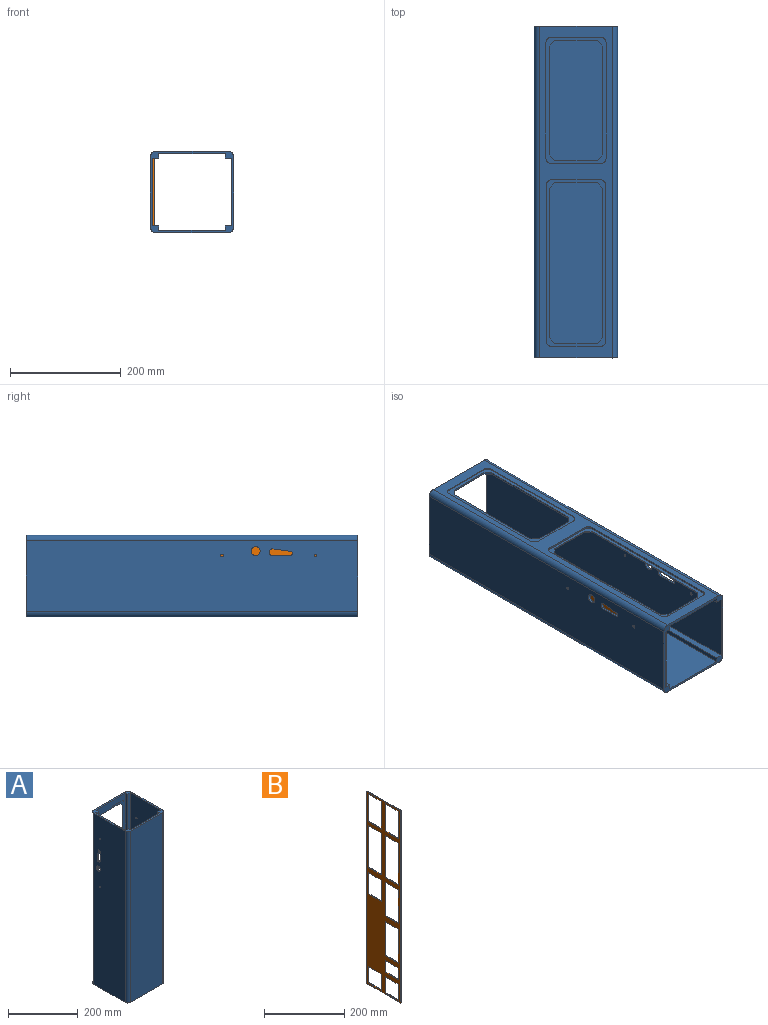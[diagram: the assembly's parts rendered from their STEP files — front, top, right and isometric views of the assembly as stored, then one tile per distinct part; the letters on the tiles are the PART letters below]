
ASSEMBLY  parts=2 mates=1
PART A: 70 faces, bbox 150.5x147.9x600 mm
  f0: plane 600x130.47mm, normal (0,1,0), area 21053.1mm2, adj f1,f19,f20,f21,f22,f23,f24,f25
  f1: cylinder r=10mm len=600mm, axis (0,0,-1), area 9424.8mm2, adj f0,f2,f20,f21
  f2: plane 600x127.9mm, normal (-1,0,0), area 76086.2mm2, adj f1,f3,f20,f21,f56,f57,f58,f59
  f3: cylinder r=10mm len=600mm, axis (0,0,-1), area 9424.8mm2, adj f2,f4,f20,f21
  f4: plane 600x130.47mm, normal (0,-1,0), area 78281.8mm2, adj f3,f5,f20,f21
  f5: cylinder r=10mm len=600mm, axis (0,0,-1), area 9424.8mm2, adj f4,f6,f20,f21
  f6: plane 600x127.9mm, normal (1,0,0), area 76086.2mm2, adj f5,f19,f20,f21,f63,f64,f65,f66
  f7: plane 600x8.22mm, normal (1,0,0), area 4932mm2, adj f8,f18,f20,f21
  f8: plane 600x119.67mm, normal (0,-1,0), area 23393.6mm2, adj f7,f9,f20,f21,f31,f32,f33,f34
  f9: plane 600x8.22mm, normal (-1,0,0), area 4932mm2, adj f8,f10,f20,f21
  f10: plane 600x11.05mm, normal (0,-1,0), area 6630mm2, adj f9,f11,f20,f21
  f11: plane 600x122.76mm, normal (-1,0,0), area 73002.2mm2, adj f10,f12,f20,f21,f63,f64,f65,f66
  f12: plane 600x11.05mm, normal (0,1,0), area 6630mm2, adj f11,f13,f20,f21
  f13: plane 600x8.22mm, normal (-1,0,0), area 4932mm2, adj f12,f14,f20,f21
  f14: plane 600x119.67mm, normal (0,1,0), area 71801.8mm2, adj f13,f15,f20,f21
  f15: plane 600x8.22mm, normal (1,0,0), area 4932mm2, adj f14,f16,f20,f21
  f16: plane 600x11.05mm, normal (0,1,0), area 6630mm2, adj f15,f17,f20,f21
  f17: plane 600x122.76mm, normal (1,0,0), area 73002.2mm2, adj f16,f18,f20,f21,f56,f57,f58,f59
  f18: plane 600x11.05mm, normal (0,-1,0), area 6630mm2, adj f7,f17,f20,f21
  f19: cylinder r=10mm len=600mm, axis (0,0,-1), area 9424.8mm2, adj f0,f6,f20,f21
  f20: plane 150.47x147.9mm, normal (0,0,1), area 2797.6mm2, adj f0,f1,f2,f3,f4,f5,f6,f7
  f21: plane 150.47x147.9mm, normal (0,0,-1), area 2797.6mm2, adj f0,f1,f2,f3,f4,f5,f6,f7
  f22: plane 208.6x1.35mm, normal (1,0,0), area 281.6mm2, adj f0,f23,f29,f30
  f23: cylinder r=10mm len=10mm, axis (0,1,0), area 21.2mm2, adj f0,f22,f24,f30
  f24: plane 88.66x1.35mm, normal (0,0,-1), area 119.7mm2, adj f0,f23,f25,f30
  f25: cylinder r=10mm len=10mm, axis (0,1,0), area 21.2mm2, adj f0,f24,f26,f30
  f26: plane 208.6x1.35mm, normal (-1,0,0), area 281.6mm2, adj f0,f25,f27,f30
  f27: cylinder r=10mm len=10mm, axis (0,1,0), area 21.2mm2, adj f0,f26,f28,f30
  f28: plane 88.66x1.35mm, normal (0,0,1), area 119.7mm2, adj f0,f27,f29,f30
  f29: cylinder r=10mm len=10mm, axis (0,1,0), area 21.2mm2, adj f0,f22,f28,f30
  f30: plane 228.6x108.66mm, normal (0,1,0), area 4041.3mm2, adj f22,f23,f24,f25,f26,f27,f28,f29
  f31: plane 76.46x3mm, normal (0,0,1), area 229.4mm2, adj f8,f30,f32,f38
  f32: plane 10x10mm, normal (-0.71,0,0.71), area 42.4mm2, adj f8,f30,f31,f33
  f33: plane 196.8x3mm, normal (-1,0,0), area 590.4mm2, adj f8,f30,f32,f34
  f34: plane 10x10mm, normal (-0.71,0,-0.71), area 42.4mm2, adj f8,f30,f33,f35
  f35: plane 76.46x3mm, normal (0,0,-1), area 229.4mm2, adj f8,f30,f34,f36
  f36: plane 10x10mm, normal (0.71,0,-0.71), area 42.4mm2, adj f8,f30,f35,f37
  f37: plane 196.8x3mm, normal (1,0,0), area 590.4mm2, adj f8,f30,f36,f38
  f38: plane 10x10mm, normal (0.71,0,0.71), area 42.4mm2, adj f8,f30,f31,f37
  f39: cylinder r=10mm len=10mm, axis (0,1,0), area 47.1mm2, adj f0,f40,f46,f47
  f40: plane 87.95x3mm, normal (0,0,1), area 263.9mm2, adj f0,f39,f41,f47
  f41: cylinder r=10mm len=10mm, axis (0,1,0), area 47.1mm2, adj f0,f40,f42,f47
  f42: plane 281.63x3mm, normal (-1,0,0), area 844.9mm2, adj f0,f41,f43,f47
  f43: cylinder r=10mm len=10mm, axis (0,1,0), area 47.1mm2, adj f0,f42,f44,f47
  f44: plane 87.95x3mm, normal (0,0,-1), area 263.9mm2, adj f0,f43,f45,f47
  f45: cylinder r=10mm len=10mm, axis (0,1,0), area 47.1mm2, adj f0,f44,f46,f47
  f46: plane 281.63x3mm, normal (1,0,0), area 844.9mm2, adj f0,f39,f45,f47
  f47: plane 301.63x107.95mm, normal (0,1,0), area 4779.2mm2, adj f39,f40,f41,f42,f43,f44,f45,f46
  f48: plane 76.08x1.35mm, normal (0,0,1), area 102.7mm2, adj f8,f47,f49,f55
  f49: plane 10x10mm, normal (-0.71,0,0.71), area 19.1mm2, adj f8,f47,f48,f50
  f50: plane 270.34x1.35mm, normal (-1,0,0), area 365mm2, adj f8,f47,f49,f51
  f51: plane 10x10mm, normal (-0.71,0,-0.71), area 19.1mm2, adj f8,f47,f50,f52
  f52: plane 76.08x1.35mm, normal (0,0,-1), area 102.7mm2, adj f8,f47,f51,f53
  f53: plane 10x10mm, normal (0.71,0,-0.71), area 19.1mm2, adj f8,f47,f52,f54
  f54: plane 270.34x1.35mm, normal (1,0,0), area 365mm2, adj f8,f47,f53,f55
  f55: plane 10x10mm, normal (0.71,0,0.71), area 19.1mm2, adj f8,f47,f48,f54
  f56: cylinder r=8.15mm len=16.3mm, axis (1,0,0), area 222.8mm2, adj f2,f17
  f57: plane 30.83x4.35mm, normal (0,1,0), area 134.1mm2, adj f2,f17,f58,f60
  f58: cylinder r=6.17mm len=12.34mm, axis (1,0,0), area 93.5mm2, adj f2,f17,f57,f59
  f59: plane 30.55x4.35mm, normal (0,-0.99,-0.13), area 134.1mm2, adj f2,f17,f58,f60
  f60: cylinder r=4.05mm len=8.1mm, axis (1,0,0), area 58.5mm2, adj f2,f17,f57,f59
  f61: cylinder r=2.45mm len=4.9mm, axis (1,0,0), area 67mm2, adj f2,f17
  f62: cylinder r=2.45mm len=4.9mm, axis (1,0,0), area 67mm2, adj f2,f17
  f63: cylinder r=8.15mm len=16.3mm, axis (1,0,0), area 222.8mm2, adj f6,f11
  f64: cylinder r=4.05mm len=8.1mm, axis (1,0,0), area 58.5mm2, adj f6,f11,f65,f67
  f65: plane 30.55x4.35mm, normal (0,-0.99,-0.13), area 134.1mm2, adj f6,f11,f64,f66
  f66: cylinder r=6.17mm len=12.34mm, axis (1,0,0), area 93.5mm2, adj f6,f11,f65,f67
  f67: plane 30.83x4.35mm, normal (0,1,0), area 134.1mm2, adj f6,f11,f64,f66
  f68: cylinder r=2.45mm len=4.9mm, axis (1,0,0), area 67mm2, adj f6,f11
  f69: cylinder r=2.45mm len=4.9mm, axis (1,0,0), area 67mm2, adj f6,f11
PART B: 46 faces, bbox 2.2x119.4x585.7 mm
  f0: plane 585.72x119.4mm, normal (1,0,0), area 32163.3mm2, adj f2,f3,f4,f5,f6,f7,f8,f9
  f1: plane 585.72x119.4mm, normal (-1,0,0), area 32163.3mm2, adj f2,f3,f4,f5,f6,f7,f8,f9
  f2: plane 119.4x2.2mm, normal (0,0,1), area 262.7mm2, adj f0,f1,f3,f5
  f3: plane 585.72x2.2mm, normal (0,-1,0), area 1288.6mm2, adj f0,f1,f2,f4
  f4: plane 119.4x2.2mm, normal (0,0,-1), area 262.7mm2, adj f0,f1,f3,f5
  f5: plane 585.72x2.2mm, normal (0,1,0), area 1288.6mm2, adj f0,f1,f2,f4
  f6: plane 45.64x2.2mm, normal (0,0,-1), area 100.4mm2, adj f0,f1,f7,f9
  f7: plane 83.66x2.2mm, normal (0,1,0), area 184mm2, adj f0,f1,f6,f8
  f8: plane 45.64x2.2mm, normal (0,0,1), area 100.4mm2, adj f0,f1,f7,f9
  f9: plane 83.66x2.2mm, normal (0,-1,0), area 184mm2, adj f0,f1,f6,f8
  f10: plane 45.64x2.2mm, normal (0,0,-1), area 100.4mm2, adj f0,f1,f11,f13
  f11: plane 83.66x2.2mm, normal (0,1,0), area 184mm2, adj f0,f1,f10,f12
  f12: plane 45.64x2.2mm, normal (0,0,1), area 100.4mm2, adj f0,f1,f11,f13
  f13: plane 83.66x2.2mm, normal (0,-1,0), area 184mm2, adj f0,f1,f10,f12
  f14: plane 45.64x2.2mm, normal (0,0,-1), area 100.4mm2, adj f0,f1,f15,f17
  f15: plane 127.6x2.2mm, normal (0,1,0), area 280.7mm2, adj f0,f1,f14,f16
  f16: plane 45.64x2.2mm, normal (0,0,1), area 100.4mm2, adj f0,f1,f15,f17
  f17: plane 127.6x2.2mm, normal (0,-1,0), area 280.7mm2, adj f0,f1,f14,f16
  f18: plane 45.64x2.2mm, normal (0,0,-1), area 100.4mm2, adj f0,f1,f19,f21
  f19: plane 127.6x2.2mm, normal (0,1,0), area 280.7mm2, adj f0,f1,f18,f20
  f20: plane 45.64x2.2mm, normal (0,0,1), area 100.4mm2, adj f0,f1,f19,f21
  f21: plane 127.6x2.2mm, normal (0,-1,0), area 280.7mm2, adj f0,f1,f18,f20
  f22: plane 45.64x2.2mm, normal (0,0,-1), area 100.4mm2, adj f0,f1,f23,f25
  f23: plane 65.07x2.2mm, normal (0,1,0), area 143.1mm2, adj f0,f1,f22,f24
  f24: plane 45.64x2.2mm, normal (0,0,1), area 100.4mm2, adj f0,f1,f23,f25
  f25: plane 65.07x2.2mm, normal (0,-1,0), area 143.1mm2, adj f0,f1,f22,f24
  f26: plane 45.64x2.2mm, normal (0,0,-1), area 100.4mm2, adj f0,f1,f27,f29
  f27: plane 48.96x2.2mm, normal (0,1,0), area 107.7mm2, adj f0,f1,f26,f28
  f28: plane 45.64x2.2mm, normal (0,0,1), area 100.4mm2, adj f0,f1,f27,f29
  f29: plane 48.96x2.2mm, normal (0,-1,0), area 107.7mm2, adj f0,f1,f26,f28
  f30: plane 45.64x2.2mm, normal (0,0,-1), area 100.4mm2, adj f0,f1,f31,f33
  f31: plane 103.08x2.2mm, normal (0,1,0), area 226.8mm2, adj f0,f1,f30,f32
  f32: plane 45.64x2.2mm, normal (0,0,1), area 100.4mm2, adj f0,f1,f31,f33
  f33: plane 103.08x2.2mm, normal (0,-1,0), area 226.8mm2, adj f0,f1,f30,f32
  f34: plane 45.64x2.2mm, normal (0,0,-1), area 100.4mm2, adj f0,f1,f35,f37
  f35: plane 103.07x2.2mm, normal (0,1,0), area 226.7mm2, adj f0,f1,f34,f36
  f36: plane 45.64x2.2mm, normal (0,0,1), area 100.4mm2, adj f0,f1,f35,f37
  f37: plane 103.07x2.2mm, normal (0,-1,0), area 226.7mm2, adj f0,f1,f34,f36
  f38: plane 45.64x2.2mm, normal (0,0,-1), area 100.4mm2, adj f0,f1,f39,f41
  f39: plane 35.87x2.2mm, normal (0,1,0), area 78.9mm2, adj f0,f1,f38,f40
  f40: plane 45.64x2.2mm, normal (0,0,1), area 100.4mm2, adj f0,f1,f39,f41
  f41: plane 35.87x2.2mm, normal (0,-1,0), area 78.9mm2, adj f0,f1,f38,f40
  f42: plane 45.64x2.2mm, normal (0,0,-1), area 100.4mm2, adj f0,f1,f43,f45
  f43: plane 48.96x2.2mm, normal (0,1,0), area 107.7mm2, adj f0,f1,f42,f44
  f44: plane 45.64x2.2mm, normal (0,0,1), area 100.4mm2, adj f0,f1,f43,f45
  f45: plane 48.96x2.2mm, normal (0,-1,0), area 107.7mm2, adj f0,f1,f42,f44
PLACE A rot(axis=(1,0,0),90deg) t=(-468.11,161.33,83.71)mm
PLACE B rot(axis=(0,0.71,0.71),180deg) t=(-302,-45.56,62.63)mm
MATE planar B.f0 <-> A.f17  axis (-1,0,0) through (-304.2,-185.51,72.32)mm
